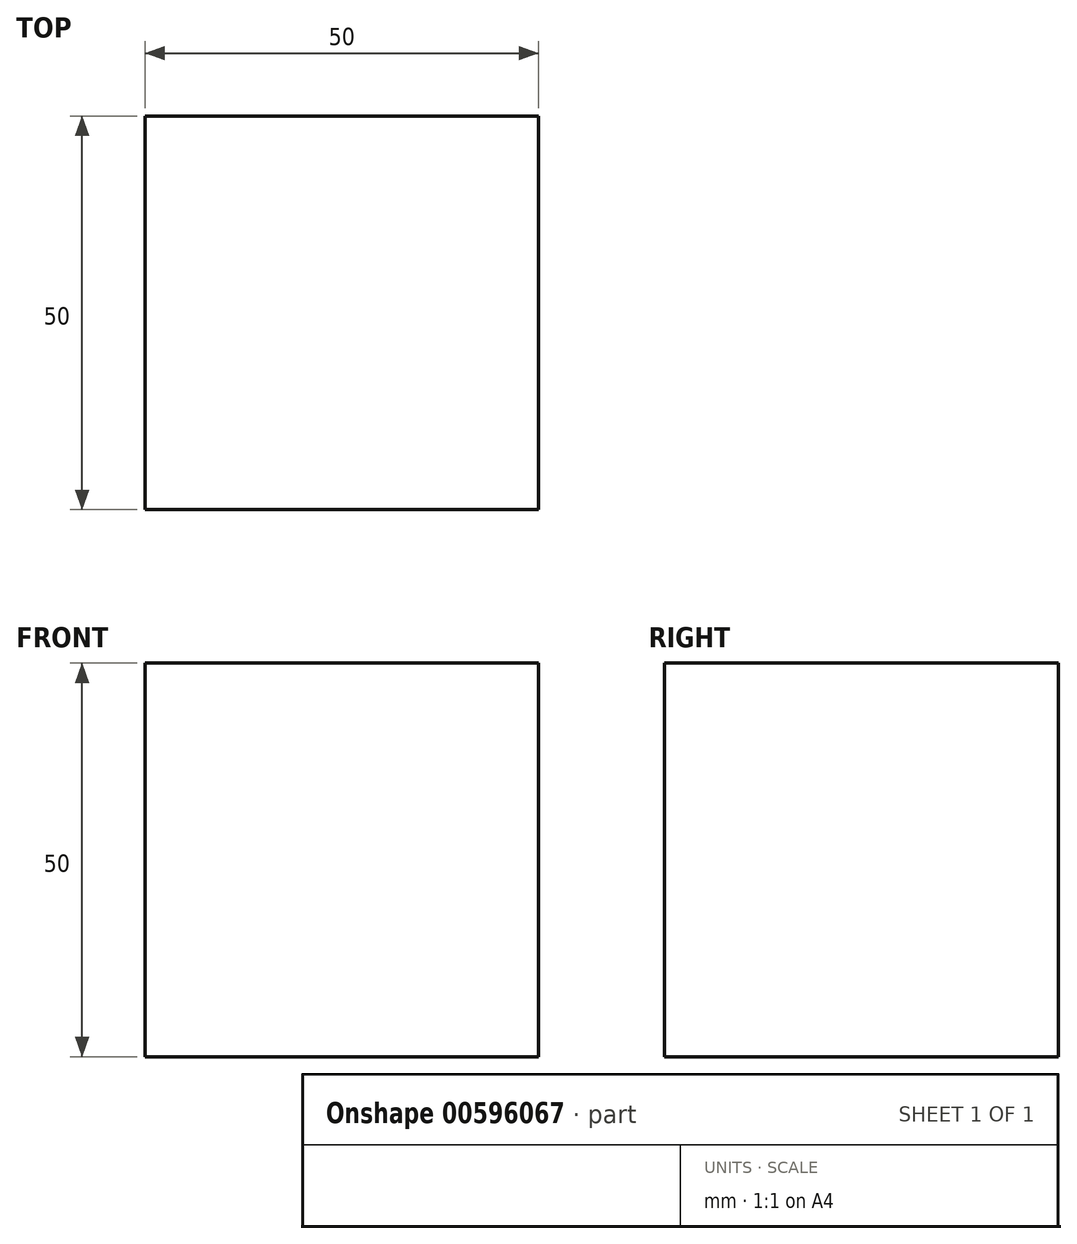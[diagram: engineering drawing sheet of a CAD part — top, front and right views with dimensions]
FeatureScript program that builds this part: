
annotation { "Feature Type Name" : "Feature", "Feature Type Description" : "" }
export const myFeature = defineFeature(function(context is Context, id is Id, definition is map)
    precondition{}
    {
        {
            var Q0;
            Q0=qCreatedBy(makeId("Top.planeOp"),FACE);
            var sketch = newSketch(context, id + "F0", { "sketchPlane" : qUnion([Q0])});
            skLineSegment(sketch, "E0.bottom", {"start": v(25, -25) * mm, "end": v(-25, -25) * mm});
            skLineSegment(sketch, "E0.top", {"start": v(25, 25) * mm, "end": v(-25, 25) * mm});
            skLineSegment(sketch, "E0.left", {"start": v(25, -25) * mm, "end": v(25, 25) * mm});
            skLineSegment(sketch, "E0.right", {"start": v(-25, -25) * mm, "end": v(-25, 25) * mm});
            skPoint(sketch, "E0.middle", {"position": v(0, 0) * mm});
            skSolve(sketch);
        }
        {
            var Q0;
            Q0=makeQuery(id+"F0.imprint","IMPRINT",FACE,{"disambiguationData":[TD([[makeQuery(id+"F0.imprint","IMPRINT",EDGE,{"derivedFrom":sQuery(id+"F0.wireOp",EDGE,"E0.bottom")}),-1.0]])]});
            extrude(context, id + "F1", {"entities" : qUnion([Q0]), "depth" : 50 * mm, "offsetDistance" : 25 * mm});
        }
    });
